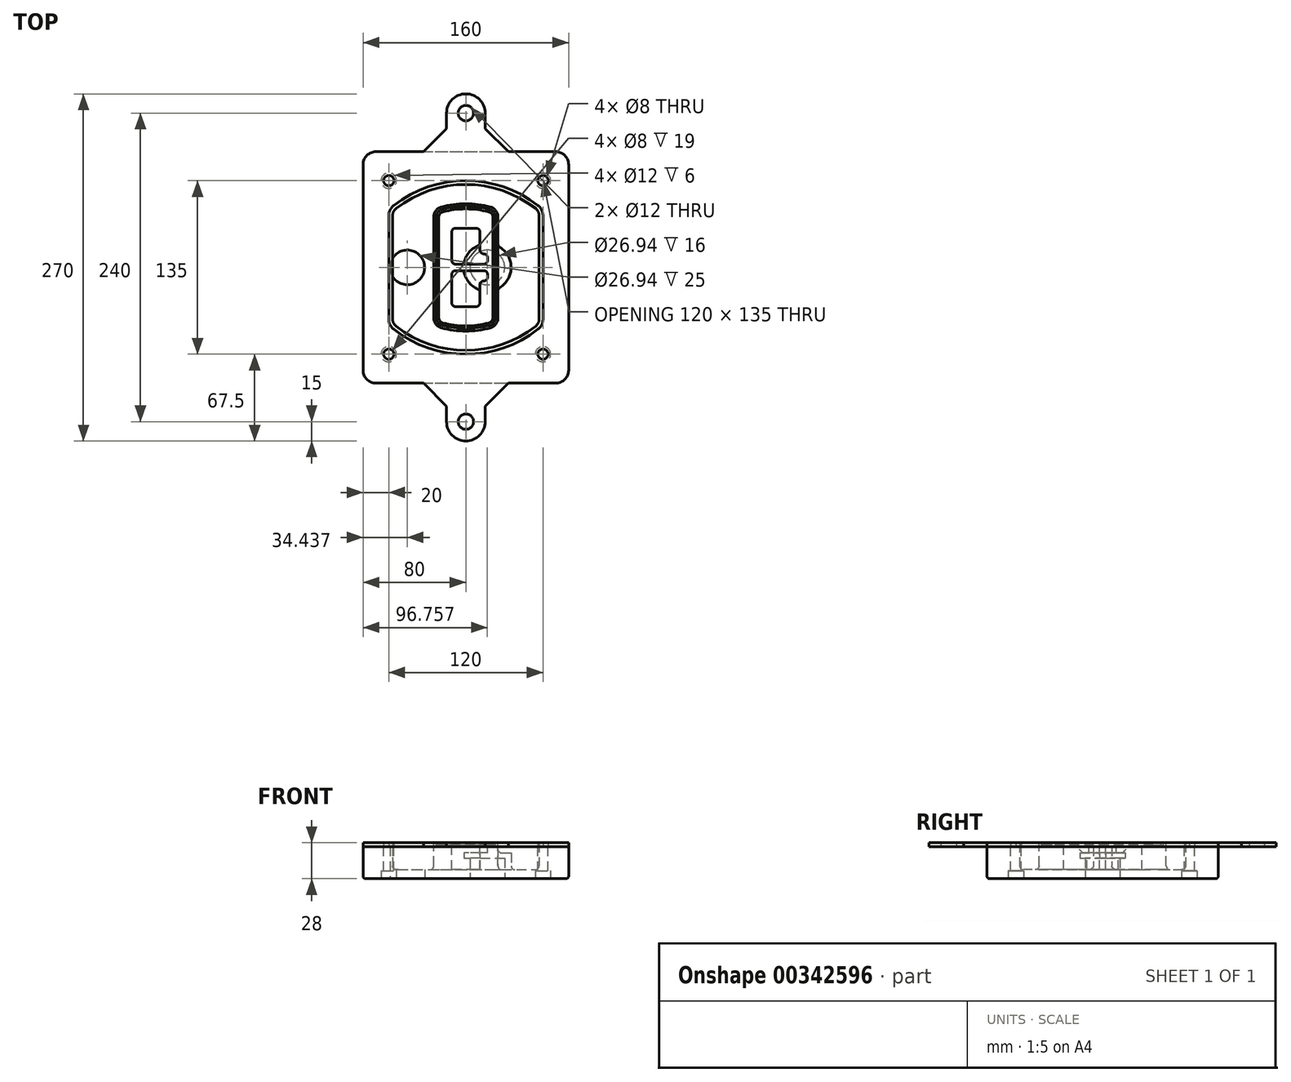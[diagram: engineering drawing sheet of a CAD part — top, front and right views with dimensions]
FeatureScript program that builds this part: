
annotation { "Feature Type Name" : "Feature", "Feature Type Description" : "" }
export const myFeature = defineFeature(function(context is Context, id is Id, definition is map)
    precondition{}
    {
        {
            var Q0;
            Q0=qCreatedBy(makeId("Top.planeOp"),FACE);
            var sketch = newSketch(context, id + "F0", { "sketchPlane" : qUnion([Q0])});
            skPoint(sketch, "E0.rect.middle", {"position": v(0, 0) * mm});
            skLineSegment(sketch, "E1.bottom", {"start": v(-70, -90) * mm, "end": v(70, -90) * mm});
            skLineSegment(sketch, "E1.top", {"start": v(-70, 90) * mm, "end": v(70, 90) * mm});
            skLineSegment(sketch, "E1.left", {"start": v(-80, -80) * mm, "end": v(-80, 80) * mm});
            skLineSegment(sketch, "E1.right", {"start": v(80, -80) * mm, "end": v(80, 80) * mm});
            skLineSegment(sketch, "E2", {"start": v(-80, 90) * mm, "end": v(80, -90) * mm, "construction": true});
            skLineSegment(sketch, "E3", {"start": v(80, 90) * mm, "end": v(-80, -90) * mm, "construction": true});
            skCircle(sketch, "E4", {"center": v(-60, 67.5) * mm, "radius": 4 * mm});
            skCircle(sketch, "E5", {"center": v(60, 67.5) * mm, "radius": 4 * mm});
            skCircle(sketch, "E6", {"center": v(60, -67.5) * mm, "radius": 4 * mm});
            skCircle(sketch, "E7", {"center": v(-60, -67.5) * mm, "radius": 4 * mm});
            skLineSegment(sketch, "E8", {"start": v(-60, 67.5) * mm, "end": v(60, 67.5) * mm, "construction": true});
            skLineSegment(sketch, "E9", {"start": v(60, 67.5) * mm, "end": v(60, -67.5) * mm, "construction": true});
            skLineSegment(sketch, "E10", {"start": v(60, -67.5) * mm, "end": v(-60, -67.5) * mm, "construction": true});
            skLineSegment(sketch, "E11", {"start": v(-60, -67.5) * mm, "end": v(-60, 67.5) * mm, "construction": true});
            skLineSegment(sketch, "E12", {"start": v(-60, 40.3) * mm, "end": v(-60, -40.3) * mm});
            skLineSegment(sketch, "E13", {"start": v(60, 40.3) * mm, "end": v(60, -40.3) * mm});
            skArc(sketch, "E14", {"start": v(56.15, 48.18) * mm, "mid": v(0, 67.5) * mm, "end": v(-56.15, 48.18) * mm});
            skArc(sketch, "E15", {"start": v(-56.15, -48.18) * mm, "mid": v(0, -67.5) * mm, "end": v(56.15, -48.18) * mm});
            skLineSegment(sketch, "E16", {"start": v(-60, 0) * mm, "end": v(60, 0) * mm, "construction": true});
            skPoint(sketch, "E17.visualSharp", {"position": v(-60, -45) * mm});
            skArc(sketch, "E17.filletArc", {"start": v(-60, -40.3) * mm, "mid": v(-58.99, -44.68) * mm, "end": v(-56.15, -48.18) * mm});
            skPoint(sketch, "E18.visualSharp", {"position": v(-60, 45) * mm});
            skArc(sketch, "E18.filletArc", {"start": v(-56.15, 48.18) * mm, "mid": v(-58.99, 44.68) * mm, "end": v(-60, 40.3) * mm});
            skPoint(sketch, "E19.visualSharp", {"position": v(60, 45) * mm});
            skArc(sketch, "E19.filletArc", {"start": v(60, 40.3) * mm, "mid": v(58.99, 44.68) * mm, "end": v(56.15, 48.18) * mm});
            skPoint(sketch, "E20.visualSharp", {"position": v(60, -45) * mm});
            skArc(sketch, "E20.filletArc", {"start": v(56.15, -48.18) * mm, "mid": v(58.99, -44.68) * mm, "end": v(60, -40.3) * mm});
            skPoint(sketch, "E21.visualSharp", {"position": v(-80, 90) * mm});
            skArc(sketch, "E21.filletArc", {"start": v(-70, 90) * mm, "mid": v(-77.07, 87.07) * mm, "end": v(-80, 80) * mm});
            skPoint(sketch, "E22.visualSharp", {"position": v(80, 90) * mm});
            skArc(sketch, "E22.filletArc", {"start": v(80, 80) * mm, "mid": v(77.07, 87.07) * mm, "end": v(70, 90) * mm});
            skPoint(sketch, "E23.visualSharp", {"position": v(80, -90) * mm});
            skArc(sketch, "E23.filletArc", {"start": v(70, -90) * mm, "mid": v(77.07, -87.07) * mm, "end": v(80, -80) * mm});
            skPoint(sketch, "E24.visualSharp", {"position": v(-80, -90) * mm});
            skArc(sketch, "E24.filletArc", {"start": v(-80, -80) * mm, "mid": v(-77.07, -87.07) * mm, "end": v(-70, -90) * mm});
            skArc(sketch, "E25.0", {"start": v(57, 40.3) * mm, "mid": v(56.3, 43.36) * mm, "end": v(54.3, 45.81) * mm});
            skLineSegment(sketch, "E25.1", {"start": v(57, 40.3) * mm, "end": v(57, -40.3) * mm});
            skArc(sketch, "E25.2", {"start": v(54.3, -45.81) * mm, "mid": v(56.3, -43.36) * mm, "end": v(57, -40.3) * mm});
            skArc(sketch, "E25.3", {"start": v(-54.3, -45.81) * mm, "mid": v(0, -64.5) * mm, "end": v(54.3, -45.81) * mm});
            skArc(sketch, "E25.4", {"start": v(-57, -40.3) * mm, "mid": v(-56.3, -43.36) * mm, "end": v(-54.3, -45.81) * mm});
            skArc(sketch, "E25.5", {"start": v(54.3, 45.81) * mm, "mid": v(0, 64.5) * mm, "end": v(-54.3, 45.81) * mm});
            skLineSegment(sketch, "E25.6", {"start": v(-57, 40.3) * mm, "end": v(-57, -40.3) * mm});
            skArc(sketch, "E25.7", {"start": v(-54.3, 45.81) * mm, "mid": v(-56.3, 43.36) * mm, "end": v(-57, 40.3) * mm});
            skArc(sketch, "E26.0", {"start": v(-58.62, 51.33) * mm, "mid": v(-62.58, 46.43) * mm, "end": v(-64, 40.3) * mm});
            skArc(sketch, "E26.1", {"start": v(58.62, 51.33) * mm, "mid": v(0, 71.5) * mm, "end": v(-58.62, 51.33) * mm});
            skArc(sketch, "E26.2", {"start": v(64, 40.3) * mm, "mid": v(62.58, 46.43) * mm, "end": v(58.62, 51.33) * mm});
            skLineSegment(sketch, "E26.3", {"start": v(64, 40.3) * mm, "end": v(64, -40.3) * mm});
            skArc(sketch, "E26.4", {"start": v(58.62, -51.33) * mm, "mid": v(62.58, -46.43) * mm, "end": v(64, -40.3) * mm});
            skLineSegment(sketch, "E26.5", {"start": v(-64, 40.3) * mm, "end": v(-64, -40.3) * mm});
            skArc(sketch, "E26.6", {"start": v(-58.62, -51.33) * mm, "mid": v(0, -71.5) * mm, "end": v(58.62, -51.33) * mm});
            skArc(sketch, "E26.7", {"start": v(-64, -40.3) * mm, "mid": v(-62.58, -46.43) * mm, "end": v(-58.62, -51.33) * mm});
            skSolve(sketch);
        }
        {
            var Q0;
            Q0=makeQuery(id+"F0.imprint","IMPRINT",FACE,{"disambiguationData":[TD([[makeQuery(id+"F0.imprint","IMPRINT",EDGE,{"derivedFrom":sQuery(id+"F0.wireOp",EDGE,"E1.bottom")}),1.0]])]});
            var Q1;
            Q1=makeQuery(id+"F0.imprint","IMPRINT",FACE,{"disambiguationData":[TD([[makeQuery(id+"F0.imprint","IMPRINT",EDGE,{"derivedFrom":sQuery(id+"F0.wireOp",EDGE,"E12")}),1.0]])]});
            var Q2;
            Q2=makeQuery(id+"F0.imprint","IMPRINT",FACE,{"disambiguationData":[TD([[makeQuery(id+"F0.imprint","IMPRINT",EDGE,{"derivedFrom":sQuery(id+"F0.wireOp",EDGE,"E25.0")}),1.0]])]});
            var Q3;
            Q3=makeQuery(id+"F0.imprint","IMPRINT",FACE,{"disambiguationData":[TD([[makeQuery(id+"F0.imprint","IMPRINT",EDGE,{"derivedFrom":sQuery(id+"F0.wireOp",EDGE,"E12")}),-1.0]])]});
            extrude(context, id + "F1", {"entities" : qUnion([Q0, Q1, Q2, Q3]), "oppositeDirection" : true, "depth" : 25 * mm});
        }
        {
            var Q0;
            Q0=makeQuery(id+"F0.imprint","IMPRINT",FACE,{"disambiguationData":[TD([[makeQuery(id+"F0.imprint","IMPRINT",EDGE,{"derivedFrom":sQuery(id+"F0.wireOp",EDGE,"E12")}),1.0]])]});
            extrude(context, id + "F2", {"entities" : qUnion([Q0]), "operationType" : NewBodyOperationType.ADD, "depth" : 3 * mm});
        }
        {
            var Q0;
            Q0=makeQuery(id+"F0.imprint","IMPRINT",FACE,{"disambiguationData":[TD([[makeQuery(id+"F0.imprint","IMPRINT",EDGE,{"derivedFrom":sQuery(id+"F0.wireOp",EDGE,"E25.0")}),1.0]])]});
            extrude(context, id + "F3", {"entities" : qUnion([Q0]), "operationType" : NewBodyOperationType.REMOVE, "oppositeDirection" : true, "depth" : 18 * mm});
        }
        {
            var Q0;
            Q0=makeQuery(id+"F2.opExtrude","CAP_FACE",FACE,{"disambiguationData":[OSD([sQuery(id+"F0.wireOp",EDGE,"E12"),sQuery(id+"F0.wireOp",EDGE,"E13"),sQuery(id+"F0.wireOp",EDGE,"E14"),sQuery(id+"F0.wireOp",EDGE,"E15"),sQuery(id+"F0.wireOp",EDGE,"E17.filletArc"),sQuery(id+"F0.wireOp",EDGE,"E18.filletArc"),sQuery(id+"F0.wireOp",EDGE,"E19.filletArc"),sQuery(id+"F0.wireOp",EDGE,"E20.filletArc"),sQuery(id+"F0.wireOp",EDGE,"E25.0"),sQuery(id+"F0.wireOp",EDGE,"E25.1"),sQuery(id+"F0.wireOp",EDGE,"E25.2"),sQuery(id+"F0.wireOp",EDGE,"E25.3"),sQuery(id+"F0.wireOp",EDGE,"E25.4"),sQuery(id+"F0.wireOp",EDGE,"E25.5"),sQuery(id+"F0.wireOp",EDGE,"E25.6"),sQuery(id+"F0.wireOp",EDGE,"E25.7")])],"isStart":false});
            var sketch = newSketch(context, id + "F4", { "sketchPlane" : qUnion([Q0])});
            skArc(sketch, "E27.0", {"start": v(-19.08, -46.97) * mm, "mid": v(0, -49.5) * mm, "end": v(19.08, -46.97) * mm});
            skArc(sketch, "E28.0", {"start": v(19.08, 46.97) * mm, "mid": v(0, 49.5) * mm, "end": v(-19.08, 46.97) * mm});
            skLineSegment(sketch, "E29", {"start": v(-25, 39.25) * mm, "end": v(-25, -39.25) * mm});
            skLineSegment(sketch, "E30", {"start": v(25, 39.25) * mm, "end": v(25, -39.25) * mm});
            skLineSegment(sketch, "E31", {"start": v(-25, 45.1) * mm, "end": v(25, 45.1) * mm, "construction": true});
            skLineSegment(sketch, "E32", {"start": v(-25, -45.1) * mm, "end": v(25, -45.1) * mm, "construction": true});
            skPoint(sketch, "E33.visualSharp", {"position": v(-25, 45.1) * mm});
            skArc(sketch, "E33.filletArc", {"start": v(-19.08, 46.97) * mm, "mid": v(-23.35, 44.11) * mm, "end": v(-25, 39.25) * mm});
            skPoint(sketch, "E34.visualSharp", {"position": v(25, 45.1) * mm});
            skArc(sketch, "E34.filletArc", {"start": v(25, 39.25) * mm, "mid": v(23.35, 44.11) * mm, "end": v(19.08, 46.97) * mm});
            skPoint(sketch, "E35.visualSharp", {"position": v(25, -45.1) * mm});
            skArc(sketch, "E35.filletArc", {"start": v(19.08, -46.97) * mm, "mid": v(23.35, -44.11) * mm, "end": v(25, -39.25) * mm});
            skPoint(sketch, "E36.visualSharp", {"position": v(-25, -45.1) * mm});
            skArc(sketch, "E36.filletArc", {"start": v(-25, -39.25) * mm, "mid": v(-23.35, -44.11) * mm, "end": v(-19.08, -46.97) * mm});
            skArc(sketch, "E37.0", {"start": v(54.3, 45.81) * mm, "mid": v(0, 64.5) * mm, "end": v(-54.3, 45.81) * mm});
            skArc(sketch, "E37.1", {"start": v(-54.3, 45.81) * mm, "mid": v(-56.3, 43.36) * mm, "end": v(-57, 40.3) * mm});
            skLineSegment(sketch, "E37.2", {"start": v(-57, 40.3) * mm, "end": v(-57, -40.3) * mm});
            skArc(sketch, "E37.3", {"start": v(-57, -40.3) * mm, "mid": v(-56.3, -43.36) * mm, "end": v(-54.3, -45.81) * mm});
            skArc(sketch, "E37.4", {"start": v(-54.3, -45.81) * mm, "mid": v(0, -64.5) * mm, "end": v(54.3, -45.81) * mm});
            skArc(sketch, "E37.5", {"start": v(54.3, -45.81) * mm, "mid": v(56.3, -43.36) * mm, "end": v(57, -40.3) * mm});
            skLineSegment(sketch, "E37.6", {"start": v(57, 40.3) * mm, "end": v(57, -40.3) * mm});
            skArc(sketch, "E37.7", {"start": v(57, 40.3) * mm, "mid": v(56.3, 43.36) * mm, "end": v(54.3, 45.81) * mm});
            skLineSegment(sketch, "E38.0", {"start": v(23, 39.25) * mm, "end": v(23, -39.25) * mm});
            skArc(sketch, "E38.1", {"start": v(18.56, -45.04) * mm, "mid": v(21.76, -42.9) * mm, "end": v(23, -39.25) * mm});
            skArc(sketch, "E38.2", {"start": v(-18.56, -45.04) * mm, "mid": v(0, -47.5) * mm, "end": v(18.56, -45.04) * mm});
            skArc(sketch, "E38.3", {"start": v(-23, -39.25) * mm, "mid": v(-21.76, -42.9) * mm, "end": v(-18.56, -45.04) * mm});
            skLineSegment(sketch, "E38.4", {"start": v(-23, 39.25) * mm, "end": v(-23, -39.25) * mm});
            skArc(sketch, "E38.5", {"start": v(23, 39.25) * mm, "mid": v(21.76, 42.9) * mm, "end": v(18.56, 45.04) * mm});
            skArc(sketch, "E38.6", {"start": v(-18.56, 45.04) * mm, "mid": v(-21.76, 42.9) * mm, "end": v(-23, 39.25) * mm});
            skArc(sketch, "E38.7", {"start": v(18.56, 45.04) * mm, "mid": v(0, 47.5) * mm, "end": v(-18.56, 45.04) * mm});
            skArc(sketch, "E39.0", {"start": v(21, 39.25) * mm, "mid": v(20.18, 41.68) * mm, "end": v(18.04, 43.1) * mm});
            skLineSegment(sketch, "E39.1", {"start": v(21, 39.25) * mm, "end": v(21, -39.25) * mm});
            skArc(sketch, "E39.2", {"start": v(18.04, -43.1) * mm, "mid": v(20.18, -41.68) * mm, "end": v(21, -39.25) * mm});
            skArc(sketch, "E39.3", {"start": v(-18.04, -43.1) * mm, "mid": v(0, -45.5) * mm, "end": v(18.04, -43.1) * mm});
            skArc(sketch, "E39.4", {"start": v(-21, -39.25) * mm, "mid": v(-20.18, -41.68) * mm, "end": v(-18.04, -43.1) * mm});
            skArc(sketch, "E39.5", {"start": v(18.04, 43.1) * mm, "mid": v(0, 45.5) * mm, "end": v(-18.04, 43.1) * mm});
            skLineSegment(sketch, "E39.6", {"start": v(-21, 39.25) * mm, "end": v(-21, -39.25) * mm});
            skArc(sketch, "E39.7", {"start": v(-18.04, 43.1) * mm, "mid": v(-20.18, 41.68) * mm, "end": v(-21, 39.25) * mm});
            skLineSegment(sketch, "E40", {"start": v(-25, 0) * mm, "end": v(25, 0) * mm, "construction": true});
            skLineSegment(sketch, "E41", {"start": v(-11, 5.5) * mm, "end": v(-11, 27.5) * mm});
            skLineSegment(sketch, "E42", {"start": v(-8, 30.5) * mm, "end": v(8, 30.5) * mm});
            skLineSegment(sketch, "E43", {"start": v(11, 27.5) * mm, "end": v(11, 13.5) * mm});
            skLineSegment(sketch, "E44", {"start": v(14, 10.5) * mm, "end": v(14, 10.5) * mm});
            skLineSegment(sketch, "E45", {"start": v(17, 7.5) * mm, "end": v(17, 5.5) * mm});
            skLineSegment(sketch, "E46", {"start": v(14, 2.5) * mm, "end": v(-8, 2.5) * mm});
            skPoint(sketch, "E47.visualSharp", {"position": v(-11, 30.5) * mm});
            skArc(sketch, "E47.filletArc", {"start": v(-8, 30.5) * mm, "mid": v(-10.12, 29.62) * mm, "end": v(-11, 27.5) * mm});
            skPoint(sketch, "E48.visualSharp", {"position": v(11, 30.5) * mm});
            skArc(sketch, "E48.filletArc", {"start": v(11, 27.5) * mm, "mid": v(10.12, 29.62) * mm, "end": v(8, 30.5) * mm});
            skPoint(sketch, "E49.visualSharp", {"position": v(11, 10.5) * mm});
            skArc(sketch, "E49.filletArc", {"start": v(11, 13.5) * mm, "mid": v(11.88, 11.38) * mm, "end": v(14, 10.5) * mm});
            skPoint(sketch, "E50.visualSharp", {"position": v(17, 10.5) * mm});
            skArc(sketch, "E50.filletArc", {"start": v(17, 7.5) * mm, "mid": v(16.12, 9.62) * mm, "end": v(14, 10.5) * mm});
            skPoint(sketch, "E51.visualSharp", {"position": v(17, 2.5) * mm});
            skArc(sketch, "E51.filletArc", {"start": v(14, 2.5) * mm, "mid": v(16.12, 3.38) * mm, "end": v(17, 5.5) * mm});
            skPoint(sketch, "E52.visualSharp", {"position": v(-11, 2.5) * mm});
            skArc(sketch, "E52.filletArc", {"start": v(-11, 5.5) * mm, "mid": v(-10.12, 3.38) * mm, "end": v(-8, 2.5) * mm});
            skLineSegment(sketch, "E53.0.MirrorCS", {"start": v(14, -2.5) * mm, "end": v(-8, -2.5) * mm});
            skArc(sketch, "E54.0.MirrorCS", {"start": v(-11, -5.5) * mm, "mid": v(-10.12, -3.38) * mm, "end": v(-8, -2.5) * mm});
            skLineSegment(sketch, "E55.0.MirrorCS", {"start": v(-11, -5.5) * mm, "end": v(-11, -27.5) * mm});
            skArc(sketch, "E56.0.MirrorCS", {"start": v(-8, -30.5) * mm, "mid": v(-10.12, -29.62) * mm, "end": v(-11, -27.5) * mm});
            skLineSegment(sketch, "E57.0.MirrorCS", {"start": v(-8, -30.5) * mm, "end": v(8, -30.5) * mm});
            skArc(sketch, "E58.0.MirrorCS", {"start": v(11, -27.5) * mm, "mid": v(10.12, -29.62) * mm, "end": v(8, -30.5) * mm});
            skLineSegment(sketch, "E59.0.MirrorCS", {"start": v(11, -27.5) * mm, "end": v(11, -13.5) * mm});
            skArc(sketch, "E60.0.MirrorCS", {"start": v(11, -13.5) * mm, "mid": v(11.88, -11.38) * mm, "end": v(14, -10.5) * mm});
            skArc(sketch, "E61.0.MirrorCS", {"start": v(17, -7.5) * mm, "mid": v(16.12, -9.62) * mm, "end": v(14, -10.5) * mm});
            skLineSegment(sketch, "E62.0.MirrorCS", {"start": v(17, -7.5) * mm, "end": v(17, -5.5) * mm});
            skArc(sketch, "E63.0.MirrorCS", {"start": v(14, -2.5) * mm, "mid": v(16.12, -3.38) * mm, "end": v(17, -5.5) * mm});
            skSolve(sketch);
        }
        {
            var Q0;
            Q0=makeQuery(id+"F4.imprint","IMPRINT",FACE,{"disambiguationData":[TD([[makeQuery(id+"F4.imprint","IMPRINT",EDGE,{"derivedFrom":sQuery(id+"F4.wireOp",EDGE,"E27.0")}),1.0]])]});
            var Q1;
            Q1=makeQuery(id+"F4.imprint","IMPRINT",FACE,{"disambiguationData":[TD([[makeQuery(id+"F4.imprint","IMPRINT",EDGE,{"derivedFrom":sQuery(id+"F4.wireOp",EDGE,"E38.0")}),-1.0]])]});
            var Q2;
            Q2=makeQuery(id+"F4.imprint","IMPRINT",FACE,{"disambiguationData":[TD([[makeQuery(id+"F4.imprint","IMPRINT",EDGE,{"derivedFrom":sQuery(id+"F4.wireOp",EDGE,"E39.0")}),1.0]])]});
            extrude(context, id + "F5", {"entities" : qUnion([Q0, Q1, Q2]), "operationType" : NewBodyOperationType.ADD, "endBound" : BoundingType.UP_TO_NEXT, "oppositeDirection" : true, "depth" : 25 * mm});
        }
        {
            var Q0;
            Q0=makeQuery(id+"F4.imprint","IMPRINT",FACE,{"disambiguationData":[TD([[makeQuery(id+"F4.imprint","IMPRINT",EDGE,{"derivedFrom":sQuery(id+"F4.wireOp",EDGE,"E38.0")}),-1.0]])]});
            extrude(context, id + "F6", {"entities" : qUnion([Q0]), "operationType" : NewBodyOperationType.REMOVE, "oppositeDirection" : true, "depth" : 2 * mm});
        }
        {
            var Q0;
            Q0=makeQuery(id+"F1.opExtrude","CAP_FACE",FACE,{"disambiguationData":[OSD([sQuery(id+"F0.wireOp",EDGE,"E1.bottom"),sQuery(id+"F0.wireOp",EDGE,"E1.top"),sQuery(id+"F0.wireOp",EDGE,"E1.left"),sQuery(id+"F0.wireOp",EDGE,"E1.right"),sQuery(id+"F0.wireOp",EDGE,"E4"),sQuery(id+"F0.wireOp",EDGE,"E5"),sQuery(id+"F0.wireOp",EDGE,"E6"),sQuery(id+"F0.wireOp",EDGE,"E7"),sQuery(id+"F0.wireOp",EDGE,"E21.filletArc"),sQuery(id+"F0.wireOp",EDGE,"E22.filletArc"),sQuery(id+"F0.wireOp",EDGE,"E23.filletArc"),sQuery(id+"F0.wireOp",EDGE,"E24.filletArc")])],"isStart":false});
            var sketch = newSketch(context, id + "F7", { "sketchPlane" : qUnion([Q0])});
            skCircle(sketch, "E64", {"center": v(16.76, 0) * mm, "radius": 13.47 * mm});
            skCircle(sketch, "E65", {"center": v(-45.56, 0) * mm, "radius": 13.47 * mm});
            skLineSegment(sketch, "E66", {"start": v(80, 0) * mm, "end": v(-80, 0) * mm});
            skCircle(sketch, "E67", {"center": v(16.76, 0) * mm, "radius": 18.47 * mm});
            skCircle(sketch, "E68", {"center": v(60, -67.5) * mm, "radius": 6 * mm});
            skCircle(sketch, "E69", {"center": v(-60, -67.5) * mm, "radius": 6 * mm});
            skCircle(sketch, "E70", {"center": v(-60, 67.5) * mm, "radius": 6 * mm});
            skCircle(sketch, "E71", {"center": v(60, 67.5) * mm, "radius": 6 * mm});
            skSolve(sketch);
        }
        {
            var Q0;
            {var subQ1=sQuery(id+"F7.wireOp",EDGE,"E66");var subQ4=sQuery(id+"F7.wireOp",EDGE,"E64");var subQ6=makeQuery(id+"F7.imprint","INTERSECT",VERTEX,{"disambiguationData":[OD(0.0)],"derivedFrom":[subQ4,subQ1]});Q0=makeQuery(id+"F7.imprint","IMPRINT",FACE,{"disambiguationData":[TD([[makeQuery(id+"F7.imprint","IMPRINT",EDGE,{"disambiguationData":[TD([[subQ6,-1.0]])],"derivedFrom":subQ4}),-1.0]])]});}
            var Q1;
            {var subQ0=sQuery(id+"F7.wireOp",EDGE,"E66");var subQ1=sQuery(id+"F7.wireOp",EDGE,"E64");var subQ3=makeQuery(id+"F7.imprint","INTERSECT",VERTEX,{"disambiguationData":[OD(0.0)],"derivedFrom":[subQ1,subQ0]});Q1=makeQuery(id+"F7.imprint","IMPRINT",FACE,{"disambiguationData":[TD([[makeQuery(id+"F7.imprint","IMPRINT",EDGE,{"disambiguationData":[TD([[subQ3,-1.0]])],"derivedFrom":subQ1}),1.0]])]});}
            var Q2;
            {var subQ0=sQuery(id+"F7.wireOp",EDGE,"E66");var subQ1=sQuery(id+"F7.wireOp",EDGE,"E64");var subQ3=makeQuery(id+"F7.imprint","INTERSECT",VERTEX,{"disambiguationData":[OD(0.0)],"derivedFrom":[subQ1,subQ0]});Q2=makeQuery(id+"F7.imprint","IMPRINT",FACE,{"disambiguationData":[TD([[makeQuery(id+"F7.imprint","IMPRINT",EDGE,{"disambiguationData":[TD([[subQ3,1.0]])],"derivedFrom":subQ1}),1.0]])]});}
            var Q3;
            {var subQ1=sQuery(id+"F7.wireOp",EDGE,"E66");var subQ4=sQuery(id+"F7.wireOp",EDGE,"E64");var subQ6=makeQuery(id+"F7.imprint","INTERSECT",VERTEX,{"disambiguationData":[OD(0.0)],"derivedFrom":[subQ4,subQ1]});Q3=makeQuery(id+"F7.imprint","IMPRINT",FACE,{"disambiguationData":[TD([[makeQuery(id+"F7.imprint","IMPRINT",EDGE,{"disambiguationData":[TD([[subQ6,1.0]])],"derivedFrom":subQ4}),-1.0]])]});}
            extrude(context, id + "F8", {"entities" : qUnion([Q0, Q1, Q2, Q3]), "operationType" : NewBodyOperationType.ADD, "oppositeDirection" : true, "depth" : 20 * mm});
        }
        {
            var Q0;
            {var subQ0=sQuery(id+"F7.wireOp",EDGE,"E66");var subQ1=sQuery(id+"F7.wireOp",EDGE,"E64");var subQ3=makeQuery(id+"F7.imprint","INTERSECT",VERTEX,{"disambiguationData":[OD(0.0)],"derivedFrom":[subQ1,subQ0]});Q0=makeQuery(id+"F7.imprint","IMPRINT",FACE,{"disambiguationData":[TD([[makeQuery(id+"F7.imprint","IMPRINT",EDGE,{"disambiguationData":[TD([[subQ3,-1.0]])],"derivedFrom":subQ1}),1.0]])]});}
            var Q1;
            {var subQ0=sQuery(id+"F7.wireOp",EDGE,"E66");var subQ1=sQuery(id+"F7.wireOp",EDGE,"E64");var subQ3=makeQuery(id+"F7.imprint","INTERSECT",VERTEX,{"disambiguationData":[OD(0.0)],"derivedFrom":[subQ1,subQ0]});Q1=makeQuery(id+"F7.imprint","IMPRINT",FACE,{"disambiguationData":[TD([[makeQuery(id+"F7.imprint","IMPRINT",EDGE,{"disambiguationData":[TD([[subQ3,1.0]])],"derivedFrom":subQ1}),1.0]])]});}
            extrude(context, id + "F9", {"entities" : qUnion([Q0, Q1]), "operationType" : NewBodyOperationType.REMOVE, "oppositeDirection" : true, "depth" : 16 * mm});
        }
        {
            var Q0;
            {var subQ0=sQuery(id+"F7.wireOp",EDGE,"E66");var subQ1=sQuery(id+"F7.wireOp",EDGE,"E65");var subQ3=makeQuery(id+"F7.imprint","INTERSECT",VERTEX,{"disambiguationData":[OD(0.0)],"derivedFrom":[subQ1,subQ0]});Q0=makeQuery(id+"F7.imprint","IMPRINT",FACE,{"disambiguationData":[TD([[makeQuery(id+"F7.imprint","IMPRINT",EDGE,{"disambiguationData":[TD([[subQ3,-1.0]])],"derivedFrom":subQ1}),1.0]])]});}
            var Q1;
            {var subQ0=sQuery(id+"F7.wireOp",EDGE,"E66");var subQ1=sQuery(id+"F7.wireOp",EDGE,"E65");var subQ3=makeQuery(id+"F7.imprint","INTERSECT",VERTEX,{"disambiguationData":[OD(0.0)],"derivedFrom":[subQ1,subQ0]});Q1=makeQuery(id+"F7.imprint","IMPRINT",FACE,{"disambiguationData":[TD([[makeQuery(id+"F7.imprint","IMPRINT",EDGE,{"disambiguationData":[TD([[subQ3,1.0]])],"derivedFrom":subQ1}),1.0]])]});}
            extrude(context, id + "F10", {"entities" : qUnion([Q0, Q1]), "operationType" : NewBodyOperationType.REMOVE, "oppositeDirection" : true, "depth" : 25 * mm});
        }
        {
            var Q0;
            Q0=makeQuery(id+"F7.imprint","IMPRINT",FACE,{"disambiguationData":[TD([[makeQuery(id+"F7.imprint","IMPRINT",EDGE,{"derivedFrom":sQuery(id+"F7.wireOp",EDGE,"E68")}),1.0]])]});
            var Q1;
            Q1=makeQuery(id+"F7.imprint","IMPRINT",FACE,{"disambiguationData":[TD([[makeQuery(id+"F7.imprint","IMPRINT",EDGE,{"derivedFrom":makeQuery(id+"F1.opExtrude","CAP_EDGE",EDGE,{"disambiguationData":[OSD([sQuery(id+"F0.wireOp",EDGE,"E5")])],"isStart":false})}),-1.0]])]});
            var Q2;
            Q2=makeQuery(id+"F7.imprint","IMPRINT",FACE,{"disambiguationData":[TD([[makeQuery(id+"F7.imprint","IMPRINT",EDGE,{"derivedFrom":sQuery(id+"F7.wireOp",EDGE,"E69")}),1.0]])]});
            var Q3;
            Q3=makeQuery(id+"F7.imprint","IMPRINT",FACE,{"disambiguationData":[TD([[makeQuery(id+"F7.imprint","IMPRINT",EDGE,{"derivedFrom":makeQuery(id+"F1.opExtrude","CAP_EDGE",EDGE,{"disambiguationData":[OSD([sQuery(id+"F0.wireOp",EDGE,"E4")])],"isStart":false})}),-1.0]])]});
            var Q4;
            Q4=makeQuery(id+"F7.imprint","IMPRINT",FACE,{"disambiguationData":[TD([[makeQuery(id+"F7.imprint","IMPRINT",EDGE,{"derivedFrom":sQuery(id+"F7.wireOp",EDGE,"E70")}),1.0]])]});
            var Q5;
            Q5=makeQuery(id+"F7.imprint","IMPRINT",FACE,{"disambiguationData":[TD([[makeQuery(id+"F7.imprint","IMPRINT",EDGE,{"derivedFrom":makeQuery(id+"F1.opExtrude","CAP_EDGE",EDGE,{"disambiguationData":[OSD([sQuery(id+"F0.wireOp",EDGE,"E7")])],"isStart":false})}),-1.0]])]});
            var Q6;
            Q6=makeQuery(id+"F7.imprint","IMPRINT",FACE,{"disambiguationData":[TD([[makeQuery(id+"F7.imprint","IMPRINT",EDGE,{"derivedFrom":sQuery(id+"F7.wireOp",EDGE,"E71")}),1.0]])]});
            var Q7;
            Q7=makeQuery(id+"F7.imprint","IMPRINT",FACE,{"disambiguationData":[TD([[makeQuery(id+"F7.imprint","IMPRINT",EDGE,{"derivedFrom":makeQuery(id+"F1.opExtrude","CAP_EDGE",EDGE,{"disambiguationData":[OSD([sQuery(id+"F0.wireOp",EDGE,"E6")])],"isStart":false})}),-1.0]])]});
            extrude(context, id + "F11", {"entities" : qUnion([Q0, Q1, Q2, Q3, Q4, Q5, Q6, Q7]), "operationType" : NewBodyOperationType.REMOVE, "oppositeDirection" : true, "depth" : 6 * mm});
        }
        {
            var Q0;
            Q0=makeQuery(id+"F9.boolean.opBoolean","COPY",FACE,{"derivedFrom":makeQuery(id+"F9.opExtrude","CAP_FACE",FACE,{"disambiguationData":[OSD([sQuery(id+"F7.wireOp",EDGE,"E64")])],"isStart":false})});
            var sketch = newSketch(context, id + "F12", { "sketchPlane" : qUnion([Q0])});
            skArc(sketch, "E72.0", {"start": v(11, 17.55) * mm, "mid": v(2.57, 11.82) * mm, "end": v(-1.54, 2.5) * mm});
            skArc(sketch, "E72.1", {"start": v(-1.54, -2.5) * mm, "mid": v(2.57, -11.82) * mm, "end": v(11, -17.55) * mm});
            skLineSegment(sketch, "E73", {"start": v(-1.54, -2.5) * mm, "end": v(14, -2.5) * mm});
            skLineSegment(sketch, "E74.0", {"start": v(14, 2.5) * mm, "end": v(-1.54, 2.5) * mm});
            skArc(sketch, "E74.1", {"start": v(14, 2.5) * mm, "mid": v(16.12, 3.38) * mm, "end": v(17, 5.5) * mm});
            skLineSegment(sketch, "E74.2", {"start": v(17, 7.5) * mm, "end": v(17, 5.5) * mm});
            skArc(sketch, "E74.3", {"start": v(17, 7.5) * mm, "mid": v(16.12, 9.62) * mm, "end": v(14, 10.5) * mm});
            skArc(sketch, "E74.4", {"start": v(11, 13.5) * mm, "mid": v(11.88, 11.38) * mm, "end": v(14, 10.5) * mm});
            skLineSegment(sketch, "E74.5", {"start": v(11, 17.55) * mm, "end": v(11, 13.5) * mm});
            skLineSegment(sketch, "E74.7", {"start": v(14, -2.5) * mm, "end": v(-1.54, -2.5) * mm});
            skArc(sketch, "E74.8", {"start": v(14, -2.5) * mm, "mid": v(16.12, -3.38) * mm, "end": v(17, -5.5) * mm});
            skLineSegment(sketch, "E74.9", {"start": v(17, -7.5) * mm, "end": v(17, -5.5) * mm});
            skArc(sketch, "E74.10", {"start": v(17, -7.5) * mm, "mid": v(16.12, -9.62) * mm, "end": v(14, -10.5) * mm});
            skArc(sketch, "E74.11", {"start": v(11, -13.5) * mm, "mid": v(11.88, -11.38) * mm, "end": v(14, -10.5) * mm});
            skLineSegment(sketch, "E74.12", {"start": v(11, -17.55) * mm, "end": v(11, -13.5) * mm});
            skPoint(sketch, "E75.orphan", {"position": v(11, -27.5) * mm});
            skPoint(sketch, "E76.orphan", {"position": v(-8, -2.5) * mm});
            skPoint(sketch, "E77.orphan", {"position": v(-8, 2.5) * mm});
            skPoint(sketch, "E78.orphan", {"position": v(11, 27.5) * mm});
            skSolve(sketch);
        }
        {
            var Q0;
            {var subQ7=sQuery(id+"F12.wireOp",EDGE,"E72.0");var subQ14=sQuery(id+"F12.wireOp",EDGE,"E72.1");var subQ16=sQuery(id+"F12.wireOp",EDGE,"E74.1");var subQ18=sQuery(id+"F12.wireOp",EDGE,"E74.8");Q0=qUnion([makeQuery(id+"F12.imprint","IMPRINT",FACE,{"disambiguationData":[TD([[makeQuery(id+"F12.imprint","IMPRINT",EDGE,{"derivedFrom":subQ7}),1.0]])]}),makeQuery(id+"F12.imprint","IMPRINT",FACE,{"disambiguationData":[TD([[makeQuery(id+"F12.imprint","IMPRINT",EDGE,{"derivedFrom":subQ14}),1.0]])]}),makeQuery(id+"F12.imprint","IMPRINT",FACE,{"disambiguationData":[TD([[makeQuery(id+"F12.imprint","IMPRINT",EDGE,{"derivedFrom":subQ16}),1.0]])]}),makeQuery(id+"F12.imprint","IMPRINT",FACE,{"disambiguationData":[TD([[makeQuery(id+"F12.imprint","IMPRINT",EDGE,{"derivedFrom":subQ18}),-1.0]])]})]);}
            var Q1;
            Q1=makeQuery(id+"F5.boolean.opBoolean","SPLIT",FACE,{"disambiguationData":[TD([makeQuery(id+"F5.opExtrude","SWEPT_FACE",FACE,{"disambiguationData":[OSD([sQuery(id+"F4.wireOp",EDGE,"E41")])]})])],"derivedFrom":makeQuery(id+"F3.boolean.opBoolean","COPY",FACE,{"derivedFrom":makeQuery(id+"F3.opExtrude","CAP_FACE",FACE,{"disambiguationData":[OSD([sQuery(id+"F0.wireOp",EDGE,"E25.0"),sQuery(id+"F0.wireOp",EDGE,"E25.1"),sQuery(id+"F0.wireOp",EDGE,"E25.2"),sQuery(id+"F0.wireOp",EDGE,"E25.3"),sQuery(id+"F0.wireOp",EDGE,"E25.4"),sQuery(id+"F0.wireOp",EDGE,"E25.5"),sQuery(id+"F0.wireOp",EDGE,"E25.6"),sQuery(id+"F0.wireOp",EDGE,"E25.7")])],"isStart":false})})});
            extrude(context, id + "F13", {"entities" : qUnion([Q0]), "operationType" : NewBodyOperationType.REMOVE, "endBound" : BoundingType.UP_TO_SURFACE, "endBoundEntityFace" : qUnion([Q1]), "depth" : 25 * mm});
        }
        {
            var Q0;
            Q0=makeQuery(id+"F3.boolean.opBoolean","COPY",EDGE,{"derivedFrom":makeQuery(id+"F3.opExtrude","CAP_EDGE",EDGE,{"disambiguationData":[OSD([sQuery(id+"F0.wireOp",EDGE,"E25.6")])],"isStart":false})});
            var Q1;
            Q1=makeQuery(id+"F8.boolean.opBoolean","INTERSECT",EDGE,{"derivedFrom":[makeQuery(id+"F5.opExtrude","SWEPT_FACE",FACE,{"disambiguationData":[OSD([sQuery(id+"F4.wireOp",EDGE,"E30")])]}),makeQuery(id+"F8.opExtrude","CAP_FACE",FACE,{"disambiguationData":[OSD([sQuery(id+"F7.wireOp",EDGE,"E67")])],"isStart":false})]});
            var Q2;
            Q2=makeQuery(id+"F8.boolean.opBoolean","INTERSECT",EDGE,{"disambiguationData":[OD(1.0)],"derivedFrom":[makeQuery(id+"F5.opExtrude","SWEPT_FACE",FACE,{"disambiguationData":[OSD([sQuery(id+"F4.wireOp",EDGE,"E30")])]}),makeQuery(id+"F8.opExtrude","SWEPT_FACE",FACE,{"disambiguationData":[OSD([sQuery(id+"F7.wireOp",EDGE,"E67")])]})]});
            var Q3;
            {var subQ0=sQuery(id+"F4.wireOp",EDGE,"E30");Q3=makeQuery(id+"F8.boolean.opBoolean","SPLIT",EDGE,{"disambiguationData":[TD([makeQuery(id+"F5.opExtrude","SWEPT_FACE",FACE,{"disambiguationData":[OSD([sQuery(id+"F4.wireOp",EDGE,"E35.filletArc")])]})])],"derivedFrom":makeQuery(id+"F5.opExtrude","CAP_EDGE",EDGE,{"disambiguationData":[OSD([subQ0])],"isStart":false})});}
            var Q4;
            {var subQ0=sQuery(id+"F0.wireOp",EDGE,"E25.7");var subQ1=sQuery(id+"F0.wireOp",EDGE,"E25.1");var subQ2=sQuery(id+"F0.wireOp",EDGE,"E25.6");var subQ3=sQuery(id+"F0.wireOp",EDGE,"E25.5");var subQ4=sQuery(id+"F0.wireOp",EDGE,"E25.4");var subQ5=sQuery(id+"F0.wireOp",EDGE,"E25.0");var subQ6=sQuery(id+"F0.wireOp",EDGE,"E25.2");var subQ7=sQuery(id+"F0.wireOp",EDGE,"E25.3");Q4=makeQuery(id+"F8.boolean.opBoolean","INTERSECT",EDGE,{"derivedFrom":[makeQuery(id+"F5.boolean.opBoolean","SPLIT",FACE,{"disambiguationData":[TD([makeQuery(id+"F2.opExtrude","SWEPT_FACE",FACE,{"disambiguationData":[OSD([subQ5])]})])],"derivedFrom":makeQuery(id+"F3.boolean.opBoolean","COPY",FACE,{"derivedFrom":makeQuery(id+"F3.opExtrude","CAP_FACE",FACE,{"disambiguationData":[OSD([subQ5,subQ1,subQ6,subQ7,subQ4,subQ3,subQ2,subQ0])],"isStart":false})})}),makeQuery(id+"F8.opExtrude","SWEPT_FACE",FACE,{"disambiguationData":[OSD([sQuery(id+"F7.wireOp",EDGE,"E67")])]})]});}
            var Q5;
            Q5=makeQuery(id+"F8.boolean.opBoolean","INTERSECT",EDGE,{"disambiguationData":[OD(0.0)],"derivedFrom":[makeQuery(id+"F5.opExtrude","SWEPT_FACE",FACE,{"disambiguationData":[OSD([sQuery(id+"F4.wireOp",EDGE,"E30")])]}),makeQuery(id+"F8.opExtrude","SWEPT_FACE",FACE,{"disambiguationData":[OSD([sQuery(id+"F7.wireOp",EDGE,"E67")])]})]});
            fillet(context, id + "F14", {"entities" : qUnion([Q0, Q1, Q2, Q3, Q4, Q5]), "radius" : 3 * mm, "tangentPropagation" : true, "allowEdgeOverflow" : false});
        }
        {
            var Q0;
            Q0=makeQuery(id+"F1.opExtrude","CAP_EDGE",EDGE,{"disambiguationData":[OSD([sQuery(id+"F0.wireOp",EDGE,"E1.bottom")])],"isStart":false});
            fillet(context, id + "F15", {"entities" : qUnion([Q0]), "radius" : 2 * mm, "tangentPropagation" : true, "allowEdgeOverflow" : false});
        }
        {
            var Q0;
            {var subQ0=sQuery(id+"F0.wireOp",EDGE,"E21.filletArc");var subQ1=sQuery(id+"F0.wireOp",EDGE,"E7");var subQ2=sQuery(id+"F0.wireOp",EDGE,"E6");var subQ3=sQuery(id+"F0.wireOp",EDGE,"E5");var subQ4=sQuery(id+"F0.wireOp",EDGE,"E4");var subQ5=sQuery(id+"F0.wireOp",EDGE,"E22.filletArc");var subQ6=sQuery(id+"F0.wireOp",EDGE,"E1.bottom");var subQ7=sQuery(id+"F0.wireOp",EDGE,"E1.right");var subQ8=sQuery(id+"F0.wireOp",EDGE,"E1.top");var subQ9=sQuery(id+"F0.wireOp",EDGE,"E1.left");var subQ10=sQuery(id+"F0.wireOp",EDGE,"E23.filletArc");var subQ11=sQuery(id+"F0.wireOp",EDGE,"E24.filletArc");Q0=makeQuery(id+"F2.boolean.opBoolean","SPLIT",FACE,{"disambiguationData":[TD([makeQuery(id+"F1.opExtrude","SWEPT_FACE",FACE,{"disambiguationData":[OSD([subQ6])]})])],"derivedFrom":makeQuery(id+"F1.opExtrude","CAP_FACE",FACE,{"disambiguationData":[OSD([subQ6,subQ8,subQ9,subQ7,subQ4,subQ3,subQ2,subQ1,subQ0,subQ5,subQ10,subQ11])],"isStart":true})});}
            var sketch = newSketch(context, id + "F16", { "sketchPlane" : qUnion([Q0])});
            skLineSegment(sketch, "E79.0", {"start": v(-80, -80) * mm, "end": v(-80, 80) * mm});
            skLineSegment(sketch, "E79.1", {"start": v(-70, 90) * mm, "end": v(70, 90) * mm});
            skArc(sketch, "E79.2", {"start": v(-70, 90) * mm, "mid": v(-77.07, 87.07) * mm, "end": v(-80, 80) * mm});
            skArc(sketch, "E79.3", {"start": v(80, 80) * mm, "mid": v(77.07, 87.07) * mm, "end": v(70, 90) * mm});
            skLineSegment(sketch, "E79.4", {"start": v(80, -80) * mm, "end": v(80, 80) * mm});
            skArc(sketch, "E79.5", {"start": v(70, -90) * mm, "mid": v(77.07, -87.07) * mm, "end": v(80, -80) * mm});
            skLineSegment(sketch, "E79.6", {"start": v(-70, -90) * mm, "end": v(70, -90) * mm});
            skArc(sketch, "E79.7", {"start": v(-80, -80) * mm, "mid": v(-77.07, -87.07) * mm, "end": v(-70, -90) * mm});
            skCircle(sketch, "E79.8", {"center": v(60, -67.5) * mm, "radius": 4 * mm});
            skCircle(sketch, "E79.9", {"center": v(-60, -67.5) * mm, "radius": 4 * mm});
            skCircle(sketch, "E79.10", {"center": v(-60, 67.5) * mm, "radius": 4 * mm});
            skCircle(sketch, "E79.11", {"center": v(60, 67.5) * mm, "radius": 4 * mm});
            skLineSegment(sketch, "E79.12", {"start": v(60, 40.3) * mm, "end": v(60, -40.3) * mm});
            skArc(sketch, "E79.13", {"start": v(-56.15, -48.18) * mm, "mid": v(0, -67.5) * mm, "end": v(56.15, -48.18) * mm});
            skArc(sketch, "E79.14", {"start": v(56.15, -48.18) * mm, "mid": v(58.99, -44.68) * mm, "end": v(60, -40.3) * mm});
            skArc(sketch, "E79.15", {"start": v(56.15, 48.18) * mm, "mid": v(0, 67.5) * mm, "end": v(-56.15, 48.18) * mm});
            skArc(sketch, "E79.16", {"start": v(60, 40.3) * mm, "mid": v(58.99, 44.68) * mm, "end": v(56.15, 48.18) * mm});
            skLineSegment(sketch, "E79.17", {"start": v(-60, 40.3) * mm, "end": v(-60, -40.3) * mm});
            skArc(sketch, "E79.18", {"start": v(-56.15, 48.18) * mm, "mid": v(-58.99, 44.68) * mm, "end": v(-60, 40.3) * mm});
            skArc(sketch, "E79.19", {"start": v(-60, -40.3) * mm, "mid": v(-58.99, -44.68) * mm, "end": v(-56.15, -48.18) * mm});
            skLineSegment(sketch, "E80", {"start": v(0, 90) * mm, "end": v(0, 120) * mm, "construction": true});
            skPoint(sketch, "E80.endSnap0", {"position": v(0, 90) * mm});
            skCircle(sketch, "E81", {"center": v(0, 120) * mm, "radius": 6 * mm});
            skLineSegment(sketch, "E82", {"start": v(-33, 90) * mm, "end": v(-15, 108) * mm});
            skLineSegment(sketch, "E83", {"start": v(-15, 108) * mm, "end": v(-15, 120) * mm});
            skLineSegment(sketch, "E84", {"start": v(33, 90) * mm, "end": v(15, 108) * mm});
            skLineSegment(sketch, "E85", {"start": v(15, 108) * mm, "end": v(15, 120) * mm});
            skArc(sketch, "E86", {"start": v(15, 120) * mm, "mid": v(0, 135) * mm, "end": v(-15, 120) * mm});
            skLineSegment(sketch, "E87", {"start": v(-80, 0) * mm, "end": v(80, 0) * mm, "construction": true});
            skLineSegment(sketch, "E88.MirrorCS", {"start": v(-33, -90) * mm, "end": v(-15, -108) * mm});
            skLineSegment(sketch, "E89.MirrorCS", {"start": v(-15, -108) * mm, "end": v(-15, -120) * mm});
            skArc(sketch, "E90.MirrorCS", {"start": v(15, -120) * mm, "mid": v(0, -135) * mm, "end": v(-15, -120) * mm});
            skLineSegment(sketch, "E91.MirrorCS", {"start": v(15, -108) * mm, "end": v(15, -120) * mm});
            skLineSegment(sketch, "E92.MirrorCS", {"start": v(33, -90) * mm, "end": v(15, -108) * mm});
            skLineSegment(sketch, "E93.MirrorCS", {"start": v(0, -90) * mm, "end": v(0, -120) * mm, "construction": true});
            skCircle(sketch, "E94.MirrorC", {"center": v(0, -120) * mm, "radius": 6 * mm});
            skSolve(sketch);
        }
        {
            var Q0;
            Q0 = qSketchRegion(id + "F16", true);
            var Q1;
            Q1=makeQuery(id+"F2.opExtrude","CAP_FACE",FACE,{"disambiguationData":[OSD([sQuery(id+"F0.wireOp",EDGE,"E12"),sQuery(id+"F0.wireOp",EDGE,"E13"),sQuery(id+"F0.wireOp",EDGE,"E14"),sQuery(id+"F0.wireOp",EDGE,"E15"),sQuery(id+"F0.wireOp",EDGE,"E17.filletArc"),sQuery(id+"F0.wireOp",EDGE,"E18.filletArc"),sQuery(id+"F0.wireOp",EDGE,"E19.filletArc"),sQuery(id+"F0.wireOp",EDGE,"E20.filletArc"),sQuery(id+"F0.wireOp",EDGE,"E25.0"),sQuery(id+"F0.wireOp",EDGE,"E25.1"),sQuery(id+"F0.wireOp",EDGE,"E25.2"),sQuery(id+"F0.wireOp",EDGE,"E25.3"),sQuery(id+"F0.wireOp",EDGE,"E25.4"),sQuery(id+"F0.wireOp",EDGE,"E25.5"),sQuery(id+"F0.wireOp",EDGE,"E25.6"),sQuery(id+"F0.wireOp",EDGE,"E25.7")])],"isStart":false});
            extrude(context, id + "F17", {"entities" : qUnion([Q0]), "endBound" : BoundingType.UP_TO_SURFACE, "endBoundEntityFace" : qUnion([Q1]), "depth" : 25 * mm});
        }
    });
